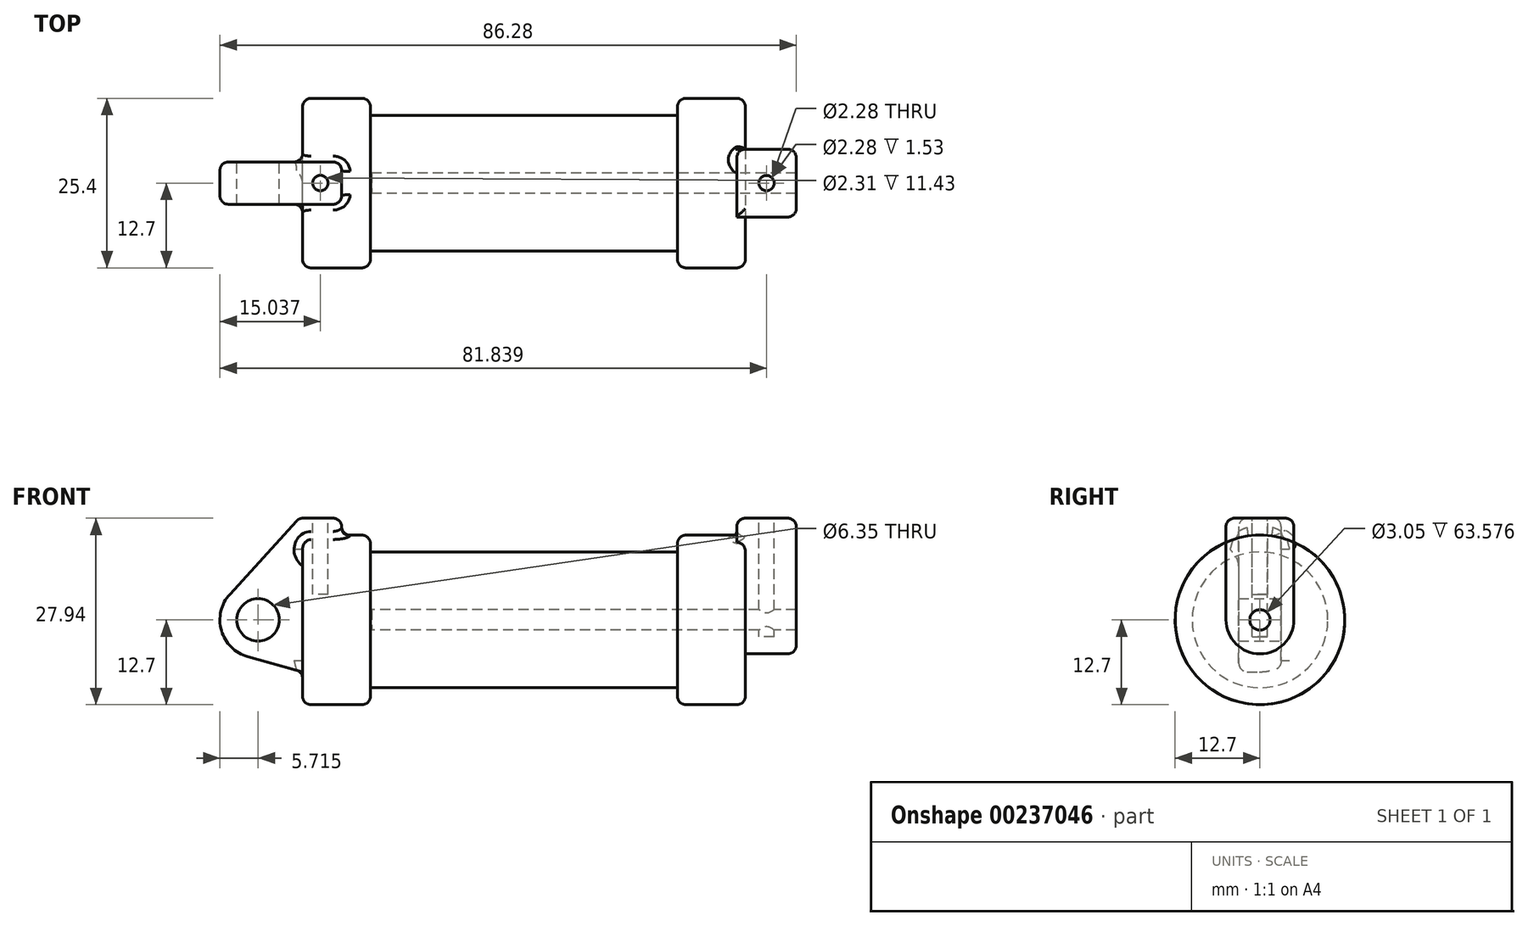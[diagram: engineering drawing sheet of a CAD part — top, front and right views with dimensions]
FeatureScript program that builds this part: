
annotation { "Feature Type Name" : "Feature", "Feature Type Description" : "" }
export const myFeature = defineFeature(function(context is Context, id is Id, definition is map)
    precondition{}
    {
        {
            var Q0;
            Q0=qCreatedBy(makeId("Front.planeOp"),FACE);
            var sketch = newSketch(context, id + "F0", { "sketchPlane" : qUnion([Q0])});
            skLineSegment(sketch, "E0", {"start": v(0, 0) * mm, "end": v(0, 12.7) * mm});
            skLineSegment(sketch, "E1", {"start": v(0, 12.7) * mm, "end": v(10.16, 12.7) * mm});
            skLineSegment(sketch, "E2", {"start": v(10.16, 12.7) * mm, "end": v(10.16, 10.16) * mm});
            skLineSegment(sketch, "E3", {"start": v(10.16, 10.16) * mm, "end": v(56.13, 10.16) * mm});
            skLineSegment(sketch, "E4", {"start": v(56.13, 10.16) * mm, "end": v(56.13, 12.7) * mm});
            skLineSegment(sketch, "E5", {"start": v(56.13, 12.7) * mm, "end": v(66.3, 12.7) * mm});
            skLineSegment(sketch, "E6", {"start": v(66.3, 12.7) * mm, "end": v(66.3, 0) * mm});
            skLineSegment(sketch, "E7", {"start": v(66.3, 0) * mm, "end": v(0, 0) * mm});
            skLineSegment(sketch, "E8", {"start": v(5.84, 15.24) * mm, "end": v(-0.5, 15.24) * mm});
            skLineSegment(sketch, "E9", {"start": v(-0.5, 15.24) * mm, "end": v(-10.88, 3.85) * mm});
            skLineSegment(sketch, "E10", {"start": v(0, 0) * mm, "end": v(-6.65, 0) * mm});
            skCircle(sketch, "E11", {"center": v(-6.65, 0) * mm, "radius": 5.72 * mm});
            skCircle(sketch, "E12", {"center": v(-6.65, 0) * mm, "radius": 3.18 * mm});
            skLineSegment(sketch, "E13", {"start": v(5.84, 15.24) * mm, "end": v(5.84, -9.4) * mm});
            skLineSegment(sketch, "E14", {"start": v(5.84, -9.4) * mm, "end": v(-8.18, -5.5) * mm});
            skSolve(sketch);
        }
        {
            var Q0;
            {var subQ0=sQuery(id+"F0.wireOp",EDGE,"E2");Q0=makeQuery(id+"F0.imprint","IMPRINT",FACE,{"disambiguationData":[TD([[makeQuery(id+"F0.imprint","IMPRINT",EDGE,{"derivedFrom":subQ0}),-1.0]])]});}
            var Q1;
            {var subQ0=sQuery(id+"F0.wireOp",EDGE,"E0");Q1=makeQuery(id+"F0.imprint","IMPRINT",FACE,{"disambiguationData":[TD([[makeQuery(id+"F0.imprint","IMPRINT",EDGE,{"derivedFrom":subQ0}),-1.0]])]});}
            var Q2;
            Q2=sQuery(id+"F0.wireOp",EDGE,"E7");
            revolve(context, id + "F1", {"entities" : qUnion([Q0, Q1]), "axis" : qUnion([Q2]), "revolveType" : RevolveType.FULL});
        }
        {
            var Q0;
            {var subQ0=sQuery(id+"F0.wireOp",EDGE,"E0");Q0=makeQuery(id+"F0.imprint","IMPRINT",FACE,{"disambiguationData":[TD([[makeQuery(id+"F0.imprint","IMPRINT",EDGE,{"derivedFrom":subQ0}),-1.0]])]});}
            var Q1;
            {var subQ3=sQuery(id+"F0.wireOp",EDGE,"E0");Q1=makeQuery(id+"F0.imprint","IMPRINT",FACE,{"disambiguationData":[TD([[makeQuery(id+"F0.imprint","IMPRINT",EDGE,{"derivedFrom":subQ3}),1.0]])]});}
            var Q2;
            {var subQ0=sQuery(id+"F0.wireOp",EDGE,"E14");Q2=makeQuery(id+"F0.imprint","IMPRINT",FACE,{"disambiguationData":[TD([[makeQuery(id+"F0.imprint","IMPRINT",EDGE,{"derivedFrom":subQ0}),-1.0]])]});}
            var Q3;
            {var subQ4=sQuery(id+"F0.wireOp",EDGE,"E12");Q3=makeQuery(id+"F0.imprint","IMPRINT",FACE,{"disambiguationData":[TD([[makeQuery(id+"F0.imprint","IMPRINT",EDGE,{"derivedFrom":subQ4}),-1.0]])]});}
            extrude(context, id + "F2", {"entities" : qUnion([Q0, Q1, Q2, Q3]), "operationType" : NewBodyOperationType.ADD, "endBound" : BoundingType.SYMMETRIC, "depth" : 6.35 * mm});
        }
        {
            var Q0;
            Q0=makeQuery(id+"F1.opRevolve","SWEPT_FACE",FACE,{"disambiguationData":[OSD([sQuery(id+"F0.wireOp",EDGE,"E6")])]});
            var sketch = newSketch(context, id + "F3", { "sketchPlane" : qUnion([Q0])});
            skCircle(sketch, "E15", {"center": v(0, 0) * mm, "radius": 5.08 * mm});
            skCircle(sketch, "E16", {"center": v(0, 0) * mm, "radius": 1.52 * mm});
            skLineSegment(sketch, "E17", {"start": v(-5.08, 0) * mm, "end": v(-5.08, 15.24) * mm});
            skLineSegment(sketch, "E18", {"start": v(5.08, 0) * mm, "end": v(5.08, 15.24) * mm});
            skLineSegment(sketch, "E19", {"start": v(5.08, 15.24) * mm, "end": v(-5.08, 15.24) * mm});
            skSolve(sketch);
        }
        {
            var Q0;
            Q0=makeQuery(id+"F3.imprint","IMPRINT",FACE,{"disambiguationData":[TD([[makeQuery(id+"F3.imprint","IMPRINT",EDGE,{"derivedFrom":sQuery(id+"F3.wireOp",EDGE,"E16")}),-1.0]])]});
            var Q1;
            {var subQ0=sQuery(id+"F3.wireOp",EDGE,"E17");var subQ1=sQuery(id+"F3.wireOp",EDGE,"E15");var subQ2=makeQuery(id+"F3.imprint","INTERSECT",VERTEX,{"derivedFrom":[subQ1,subQ0]});Q1=makeQuery(id+"F3.imprint","IMPRINT",FACE,{"disambiguationData":[TD([[makeQuery(id+"F3.imprint","IMPRINT",EDGE,{"disambiguationData":[TD([[subQ2,1.0]])],"derivedFrom":subQ1}),-1.0]])]});}
            var Q2;
            {var subQ0=sQuery(id+"F3.wireOp",EDGE,"E19");Q2=makeQuery(id+"F3.imprint","IMPRINT",FACE,{"disambiguationData":[TD([[makeQuery(id+"F3.imprint","IMPRINT",EDGE,{"derivedFrom":subQ0}),1.0]])]});}
            extrude(context, id + "F4", {"entities" : qUnion([Q0, Q1, Q2]), "operationType" : NewBodyOperationType.ADD, "depth" : 7.62 * mm, "hasSecondDirection" : true, "secondDirectionOppositeDirection" : true, "secondDirectionDepth" : 1.27 * mm});
        }
        {
            var Q0;
            Q0=makeQuery(id+"F4.boolean.opBoolean","SPLIT",FACE,{"disambiguationData":[TD([makeQuery(id+"F4.opExtrude","SWEPT_FACE",FACE,{"disambiguationData":[OSD([sQuery(id+"F3.wireOp",EDGE,"E16")])]})])],"derivedFrom":makeQuery(id+"F1.opRevolve","SWEPT_FACE",FACE,{"disambiguationData":[OSD([sQuery(id+"F0.wireOp",EDGE,"E6")])]})});
            extrude(context, id + "F5", {"entities" : qUnion([Q0]), "operationType" : NewBodyOperationType.REMOVE, "oppositeDirection" : true, "depth" : 55.96 * mm});
        }
        {
            var Q0;
            Q0=makeQuery(id+"F4.opExtrude","SWEPT_FACE",FACE,{"disambiguationData":[OSD([sQuery(id+"F3.wireOp",EDGE,"E19")])]});
            var sketch = newSketch(context, id + "F6", { "sketchPlane" : qUnion([Q0])});
            skCircle(sketch, "E20", {"center": v(69.47, 0) * mm, "radius": 1.14 * mm});
            skCircle(sketch, "E21", {"center": v(2.66, 0.05) * mm, "radius": 0.87 * mm});
            skSolve(sketch);
        }
        {
            var Q0;
            Q0=makeQuery(id+"F6.imprint","IMPRINT",FACE,{"disambiguationData":[TD([[makeQuery(id+"F6.imprint","IMPRINT",EDGE,{"derivedFrom":sQuery(id+"F6.wireOp",EDGE,"E20")}),1.0]])]});
            extrude(context, id + "F7", {"entities" : qUnion([Q0]), "operationType" : NewBodyOperationType.REMOVE, "oppositeDirection" : true, "depth" : 17.78 * mm});
        }
        {
            var Q0;
            Q0=makeQuery(id+"F2.opExtrude","SWEPT_FACE",FACE,{"disambiguationData":[OSD([sQuery(id+"F0.wireOp",EDGE,"E8")])]});
            var sketch = newSketch(context, id + "F8", { "sketchPlane" : qUnion([Q0])});
            skCircle(sketch, "E22", {"center": v(2.67, 0) * mm, "radius": 1.16 * mm});
            skSolve(sketch);
        }
        {
            var Q0;
            Q0 = qSketchRegion(id + "F8", true);
            extrude(context, id + "F9", {"entities" : qUnion([Q0]), "operationType" : NewBodyOperationType.REMOVE, "oppositeDirection" : true, "depth" : 11.43 * mm});
        }
        {
            var Q0;
            Q0=makeQuery(id+"F2.opExtrude","CAP_EDGE",EDGE,{"disambiguationData":[OSD([sQuery(id+"F0.wireOp",EDGE,"E13")])],"isStart":false});
            var Q1;
            Q1=makeQuery(id+"F2.boolean.opBoolean","INTERSECT",EDGE,{"derivedFrom":[makeQuery(id+"F1.opRevolve","SWEPT_FACE",FACE,{"disambiguationData":[OSD([sQuery(id+"F0.wireOp",EDGE,"E1")])]}),makeQuery(id+"F2.opExtrude","SWEPT_FACE",FACE,{"disambiguationData":[OSD([sQuery(id+"F0.wireOp",EDGE,"E13")])]})]});
            var Q2;
            Q2=makeQuery(id+"F2.opExtrude","SWEPT_EDGE",EDGE,{"disambiguationData":[OSD([sQuery(id+"F0.wireOp",EDGE,"E8"),sQuery(id+"F0.wireOp",EDGE,"E13")])]});
            var Q3;
            Q3=makeQuery(id+"F2.opExtrude","CAP_EDGE",EDGE,{"disambiguationData":[OSD([sQuery(id+"F0.wireOp",EDGE,"E13")])],"isStart":true});
            var Q4;
            Q4=makeQuery(id+"F2.opExtrude","CAP_EDGE",EDGE,{"disambiguationData":[OSD([sQuery(id+"F0.wireOp",EDGE,"E8")])],"isStart":false});
            var Q5;
            Q5=makeQuery(id+"F2.opExtrude","CAP_EDGE",EDGE,{"disambiguationData":[OSD([sQuery(id+"F0.wireOp",EDGE,"E9")])],"isStart":true});
            var Q6;
            Q6=makeQuery(id+"F2.opExtrude","SWEPT_EDGE",EDGE,{"disambiguationData":[OSD([sQuery(id+"F0.wireOp",EDGE,"E8"),sQuery(id+"F0.wireOp",EDGE,"E9")])]});
            var Q7;
            Q7=makeQuery(id+"F2.opExtrude","CAP_EDGE",EDGE,{"disambiguationData":[OSD([sQuery(id+"F0.wireOp",EDGE,"E8")])],"isStart":true});
            var Q8;
            Q8=makeQuery(id+"F2.opExtrude","CAP_EDGE",EDGE,{"disambiguationData":[OSD([sQuery(id+"F0.wireOp",EDGE,"E11")])],"isStart":true});
            var Q9;
            Q9=makeQuery(id+"F2.opExtrude","CAP_EDGE",EDGE,{"disambiguationData":[OSD([sQuery(id+"F0.wireOp",EDGE,"E14")])],"isStart":true});
            var Q10;
            Q10=makeQuery(id+"F2.boolean.opBoolean","INTERSECT",EDGE,{"derivedFrom":[makeQuery(id+"F1.opRevolve","SWEPT_FACE",FACE,{"disambiguationData":[OSD([sQuery(id+"F0.wireOp",EDGE,"E0")])]}),makeQuery(id+"F2.opExtrude","CAP_FACE",FACE,{"disambiguationData":[OSD([sQuery(id+"F0.wireOp",EDGE,"E8"),sQuery(id+"F0.wireOp",EDGE,"E9"),sQuery(id+"F0.wireOp",EDGE,"E11"),sQuery(id+"F0.wireOp",EDGE,"E12"),sQuery(id+"F0.wireOp",EDGE,"E13"),sQuery(id+"F0.wireOp",EDGE,"E14")])],"isStart":true})]});
            var Q11;
            Q11=makeQuery(id+"F2.boolean.opBoolean","INTERSECT",EDGE,{"derivedFrom":[makeQuery(id+"F1.opRevolve","SWEPT_FACE",FACE,{"disambiguationData":[OSD([sQuery(id+"F0.wireOp",EDGE,"E1")])]}),makeQuery(id+"F2.opExtrude","CAP_FACE",FACE,{"disambiguationData":[OSD([sQuery(id+"F0.wireOp",EDGE,"E8"),sQuery(id+"F0.wireOp",EDGE,"E9"),sQuery(id+"F0.wireOp",EDGE,"E11"),sQuery(id+"F0.wireOp",EDGE,"E12"),sQuery(id+"F0.wireOp",EDGE,"E13"),sQuery(id+"F0.wireOp",EDGE,"E14")])],"isStart":true})]});
            var Q12;
            Q12=makeQuery(id+"F1.opRevolve","SWEPT_FACE",FACE,{"disambiguationData":[OSD([sQuery(id+"F0.wireOp",EDGE,"E1")])]});
            var Q13;
            Q13=makeQuery(id+"F2.opExtrude","CAP_EDGE",EDGE,{"disambiguationData":[OSD([sQuery(id+"F0.wireOp",EDGE,"E9")])],"isStart":false});
            var Q14;
            Q14=makeQuery(id+"F2.opExtrude","CAP_EDGE",EDGE,{"disambiguationData":[OSD([sQuery(id+"F0.wireOp",EDGE,"E11")])],"isStart":false});
            var Q15;
            Q15=makeQuery(id+"F2.opExtrude","CAP_EDGE",EDGE,{"disambiguationData":[OSD([sQuery(id+"F0.wireOp",EDGE,"E14")])],"isStart":false});
            fillet(context, id + "F10", {"entities" : qUnion([Q0, Q1, Q2, Q3, Q4, Q5, Q6, Q7, Q8, Q9, Q10, Q11, Q12, Q13, Q14, Q15]), "radius" : 1.27 * mm, "tangentPropagation" : true, "allowEdgeOverflow" : false});
        }
        {
            var Q0;
            Q0=makeQuery(id+"F4.opExtrude","CAP_EDGE",EDGE,{"disambiguationData":[OSD([sQuery(id+"F3.wireOp",EDGE,"E19")])],"isStart":true});
            var Q1;
            Q1=makeQuery(id+"F4.opExtrude","SWEPT_EDGE",EDGE,{"disambiguationData":[OSD([sQuery(id+"F3.wireOp",EDGE,"E18"),sQuery(id+"F3.wireOp",EDGE,"E19")])]});
            var Q2;
            Q2=makeQuery(id+"F4.opExtrude","CAP_EDGE",EDGE,{"disambiguationData":[OSD([sQuery(id+"F3.wireOp",EDGE,"E19")])],"isStart":false});
            var Q3;
            Q3=makeQuery(id+"F4.opExtrude","SWEPT_EDGE",EDGE,{"disambiguationData":[OSD([sQuery(id+"F3.wireOp",EDGE,"E17"),sQuery(id+"F3.wireOp",EDGE,"E19")])]});
            var Q4;
            Q4=makeQuery(id+"F4.opExtrude","CAP_EDGE",EDGE,{"disambiguationData":[OSD([sQuery(id+"F3.wireOp",EDGE,"E18")])],"isStart":false});
            var Q5;
            Q5=makeQuery(id+"F4.boolean.opBoolean","INTERSECT",EDGE,{"derivedFrom":[makeQuery(id+"F1.opRevolve","SWEPT_FACE",FACE,{"disambiguationData":[OSD([sQuery(id+"F0.wireOp",EDGE,"E5")])]}),makeQuery(id+"F4.opExtrude","SWEPT_FACE",FACE,{"disambiguationData":[OSD([sQuery(id+"F3.wireOp",EDGE,"E18")])]})]});
            var Q6;
            Q6=makeQuery(id+"F4.opExtrude","CAP_EDGE",EDGE,{"disambiguationData":[OSD([sQuery(id+"F3.wireOp",EDGE,"E18")])],"isStart":true});
            var Q7;
            Q7=makeQuery(id+"F4.opExtrude","SWEPT_EDGE",EDGE,{"disambiguationData":[OSD([sQuery(id+"F3.wireOp",EDGE,"E15"),sQuery(id+"F3.wireOp",EDGE,"E18")])]});
            var Q8;
            Q8=makeQuery(id+"F4.opExtrude","CAP_EDGE",EDGE,{"disambiguationData":[OSD([sQuery(id+"F3.wireOp",EDGE,"E15")])],"isStart":false});
            var Q9;
            Q9=makeQuery(id+"F4.opExtrude","CAP_EDGE",EDGE,{"disambiguationData":[OSD([sQuery(id+"F3.wireOp",EDGE,"E17")])],"isStart":false});
            var Q10;
            Q10=makeQuery(id+"F1.opRevolve","SWEPT_EDGE",EDGE,{"disambiguationData":[OSD([sQuery(id+"F0.wireOp",EDGE,"E4"),sQuery(id+"F0.wireOp",EDGE,"E5")])]});
            fillet(context, id + "F11", {"entities" : qUnion([Q0, Q1, Q2, Q3, Q4, Q5, Q6, Q7, Q8, Q9, Q10]), "radius" : 1.27 * mm, "tangentPropagation" : true, "allowEdgeOverflow" : false});
        }
        {
            var Q0;
            Q0=makeQuery(id+"F1.opRevolve","SWEPT_EDGE",EDGE,{"disambiguationData":[OSD([sQuery(id+"F0.wireOp",EDGE,"E5"),sQuery(id+"F0.wireOp",EDGE,"E6")])]});
            fillet(context, id + "F12", {"entities" : qUnion([Q0]), "radius" : 1.27 * mm, "tangentPropagation" : true, "allowEdgeOverflow" : false});
        }
    });
